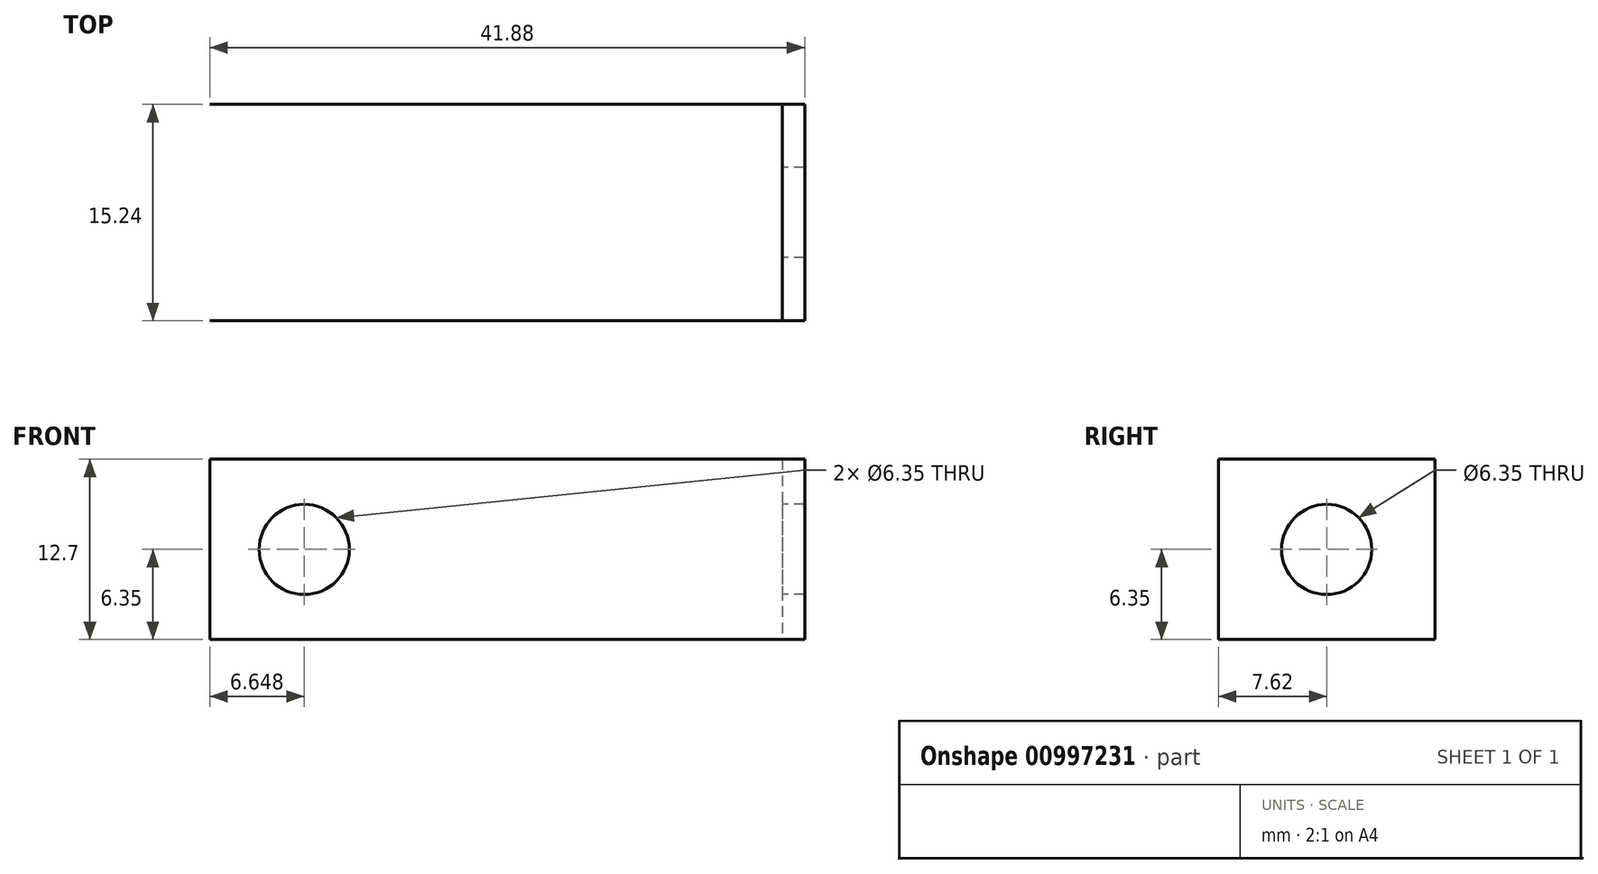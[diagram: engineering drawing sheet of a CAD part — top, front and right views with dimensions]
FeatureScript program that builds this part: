
annotation { "Feature Type Name" : "Feature", "Feature Type Description" : "" }
export const myFeature = defineFeature(function(context is Context, id is Id, definition is map)
    precondition{}
    {
        {
            var Q0;
            Q0=qCreatedBy(makeId("Front.planeOp"),FACE);
            var sketch = newSketch(context, id + "F0", { "sketchPlane" : qUnion([Q0])});
            skLineSegment(sketch, "E0.bottom", {"start": v(0, 6.35) * mm, "end": v(-40.29, 6.35) * mm});
            skLineSegment(sketch, "E0.top", {"start": v(0, -6.35) * mm, "end": v(-40.29, -6.35) * mm});
            skLineSegment(sketch, "E0.left", {"start": v(0, 6.35) * mm, "end": v(0, -6.35) * mm});
            skLineSegment(sketch, "E0.right", {"start": v(-40.29, 6.35) * mm, "end": v(-40.29, -6.35) * mm});
            skCircle(sketch, "E1", {"center": v(-33.64, 0) * mm, "radius": 3.18 * mm});
            skLineSegment(sketch, "E2", {"start": v(0, 6.35) * mm, "end": v(1.59, 6.35) * mm});
            skLineSegment(sketch, "E3", {"start": v(1.59, 6.35) * mm, "end": v(1.59, -6.35) * mm});
            skLineSegment(sketch, "E4", {"start": v(1.59, -6.35) * mm, "end": v(0, -6.35) * mm});
            skSolve(sketch);
        }
        {
            var Q0;
            Q0=makeQuery(id+"F0.imprint","IMPRINT",FACE,{"disambiguationData":[TD([[makeQuery(id+"F0.imprint","IMPRINT",EDGE,{"derivedFrom":sQuery(id+"F0.wireOp",EDGE,"E0.bottom")}),1.0]])]});
            extrude(context, id + "F1", {"entities" : qUnion([Q0]), "depth" : 1 / 406.4 * mm, "offsetDistance" : 25.4 * mm});
        }
        {
            var Q0;
            Q0=makeQuery(id+"F0.imprint","IMPRINT",FACE,{"disambiguationData":[TD([[makeQuery(id+"F0.imprint","IMPRINT",EDGE,{"derivedFrom":sQuery(id+"F0.wireOp",EDGE,"E0.left")}),1.0]])]});
            extrude(context, id + "F2", {"entities" : qUnion([Q0]), "operationType" : NewBodyOperationType.ADD, "depth" : 7.62 * mm, "offsetDistance" : 25.4 * mm});
        }
        {
            var Q0;
            Q0=makeQuery(id+"F1.opExtrude","SWEPT_BODY",BODY,{"disambiguationData":[OSD([sQuery(id+"F0.wireOp",EDGE,"E0.bottom"),sQuery(id+"F0.wireOp",EDGE,"E0.top"),sQuery(id+"F0.wireOp",EDGE,"E0.left"),sQuery(id+"F0.wireOp",EDGE,"E0.right"),sQuery(id+"F0.wireOp",EDGE,"E1")])]});
            var Q1;
            Q1=makeQuery(id+"F2.opExtrude","CAP_FACE",FACE,{"disambiguationData":[OSD([sQuery(id+"F0.wireOp",EDGE,"E0.left"),sQuery(id+"F0.wireOp",EDGE,"E2"),sQuery(id+"F0.wireOp",EDGE,"E3"),sQuery(id+"F0.wireOp",EDGE,"E4")])],"isStart":false});
            mirror(context, id + "F3", {"operationType" : NewBodyOperationType.ADD, "entities" : qUnion([Q0]), "mirrorPlane" : qUnion([Q1])});
        }
        {
            var Q0;
            {var subQ0=makeQuery(id+"F2.opExtrude","SWEPT_FACE",FACE,{"disambiguationData":[OSD([sQuery(id+"F0.wireOp",EDGE,"E0.left")])]});Q0=makeQuery(id+"F3.boolean.opBoolean","MERGE",FACE,{"derivedFrom":[subQ0,makeQuery(id+"F3.opPattern","COPY",FACE,{"derivedFrom":subQ0,"instanceName":"1"})]});}
            var sketch = newSketch(context, id + "F4", { "sketchPlane" : qUnion([Q0])});
            skCircle(sketch, "E5", {"center": v(7.62, 0) * mm, "radius": 3.18 * mm});
            skSolve(sketch);
        }
        {
            var Q0;
            Q0 = qSketchRegion(id + "F4", true);
            extrude(context, id + "F5", {"entities" : qUnion([Q0]), "operationType" : NewBodyOperationType.REMOVE, "oppositeDirection" : true, "depth" : 25.4 * mm, "offsetDistance" : 25.4 * mm});
        }
    });
